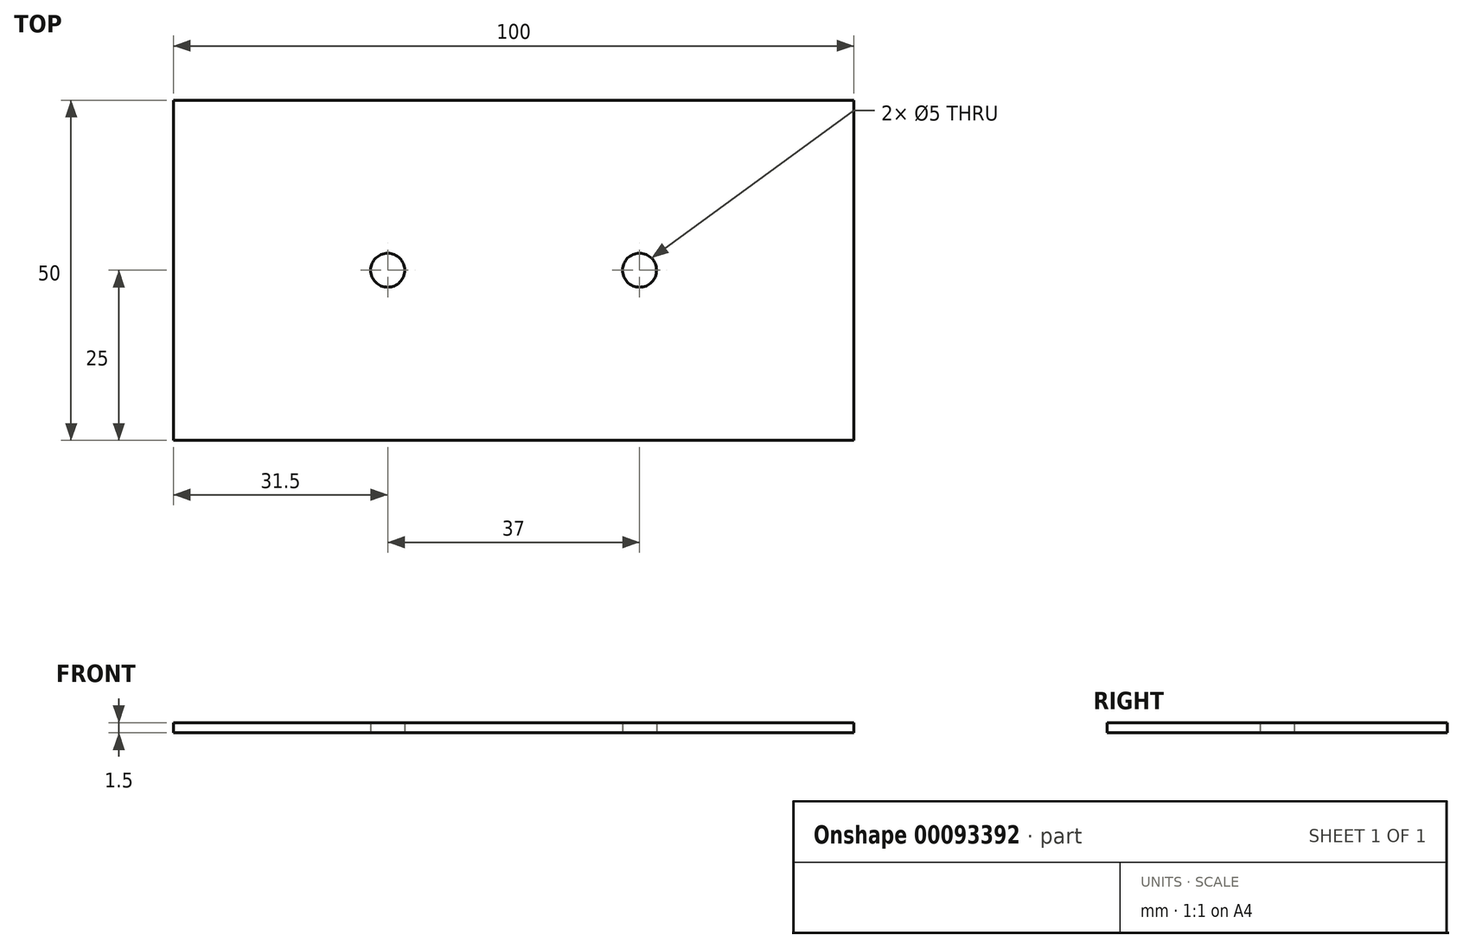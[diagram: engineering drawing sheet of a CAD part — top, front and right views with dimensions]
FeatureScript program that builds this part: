
annotation { "Feature Type Name" : "Feature", "Feature Type Description" : "" }
export const myFeature = defineFeature(function(context is Context, id is Id, definition is map)
    precondition{}
    {
        {
            var Q0;
            Q0=qCreatedBy(makeId("Top.planeOp"),FACE);
            var sketch = newSketch(context, id + "F0", { "sketchPlane" : qUnion([Q0])});
            skLineSegment(sketch, "E0.bottom", {"start": v(0, 0) * mm, "end": v(100, 0) * mm});
            skLineSegment(sketch, "E0.top", {"start": v(0, 50) * mm, "end": v(100, 50) * mm});
            skLineSegment(sketch, "E0.left", {"start": v(0, 0) * mm, "end": v(0, 50) * mm});
            skLineSegment(sketch, "E0.right", {"start": v(100, 0) * mm, "end": v(100, 50) * mm});
            skCircle(sketch, "E1", {"center": v(31.5, 25) * mm, "radius": 2.5 * mm});
            skCircle(sketch, "E2", {"center": v(68.5, 25) * mm, "radius": 2.5 * mm});
            skSolve(sketch);
        }
        {
            var Q0;
            Q0=makeQuery(id+"F0.imprint","IMPRINT",FACE,{"disambiguationData":[TD([[makeQuery(id+"F0.imprint","IMPRINT",EDGE,{"derivedFrom":sQuery(id+"F0.wireOp",EDGE,"E0.bottom")}),1.0]])]});
            extrude(context, id + "F1", {"entities" : qUnion([Q0]), "depth" : 1.5 * mm});
        }
    });
